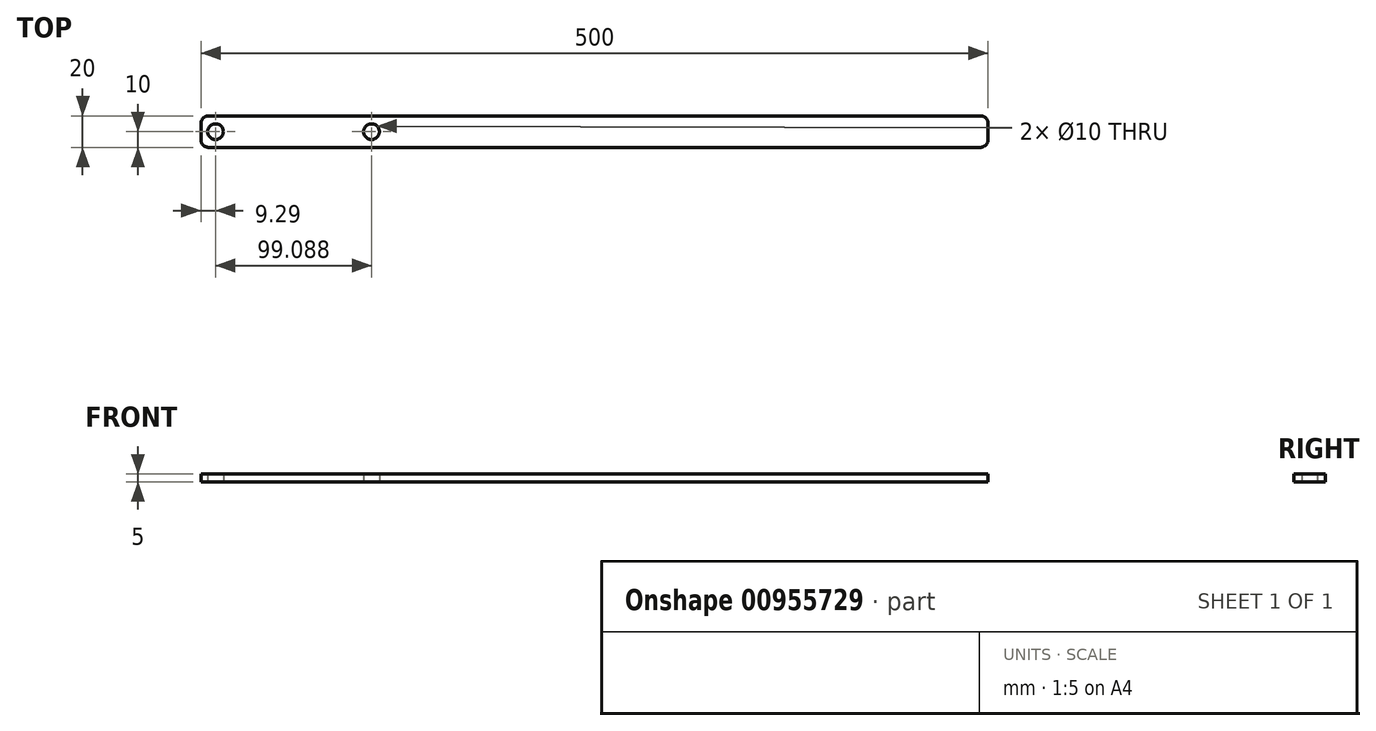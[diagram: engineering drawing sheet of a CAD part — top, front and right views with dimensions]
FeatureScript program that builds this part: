
annotation { "Feature Type Name" : "Feature", "Feature Type Description" : "" }
export const myFeature = defineFeature(function(context is Context, id is Id, definition is map)
    precondition{}
    {
        {
            var Q0;
            Q0=qCreatedBy(makeId("Top.planeOp"),FACE);
            var sketch = newSketch(context, id + "F0", { "sketchPlane" : qUnion([Q0])});
            skLineSegment(sketch, "E0.bottom", {"start": v(250, -10) * mm, "end": v(-250, -10) * mm});
            skLineSegment(sketch, "E0.top", {"start": v(250, 10) * mm, "end": v(-250, 10) * mm});
            skLineSegment(sketch, "E0.left", {"start": v(250, -10) * mm, "end": v(250, 10) * mm});
            skLineSegment(sketch, "E0.right", {"start": v(-250, -10) * mm, "end": v(-250, 10) * mm});
            skPoint(sketch, "E0.middle", {"position": v(0, 0) * mm});
            skCircle(sketch, "E1", {"center": v(-141.62, 0) * mm, "radius": 5 * mm});
            skCircle(sketch, "E2", {"center": v(-240.7, 0) * mm, "radius": 5 * mm});
            skSolve(sketch);
        }
        {
            var Q0;
            Q0=makeQuery(id+"F0.imprint","IMPRINT",FACE,{"disambiguationData":[TD([[makeQuery(id+"F0.imprint","IMPRINT",EDGE,{"derivedFrom":sQuery(id+"F0.wireOp",EDGE,"E0.bottom")}),-1.0]])]});
            extrude(context, id + "F1", {"entities" : qUnion([Q0]), "depth" : 5 * mm, "offsetDistance" : 25 * mm});
        }
        {
            var Q0;
            Q0=makeQuery(id+"F1.opExtrude","SWEPT_EDGE",EDGE,{"disambiguationData":[OSD([sQuery(id+"F0.wireOp",EDGE,"E0.bottom"),sQuery(id+"F0.wireOp",EDGE,"E0.left")])]});
            var Q1;
            Q1=makeQuery(id+"F1.opExtrude","SWEPT_EDGE",EDGE,{"disambiguationData":[OSD([sQuery(id+"F0.wireOp",EDGE,"E0.top"),sQuery(id+"F0.wireOp",EDGE,"E0.left")])]});
            var Q2;
            Q2=makeQuery(id+"F1.opExtrude","SWEPT_EDGE",EDGE,{"disambiguationData":[OSD([sQuery(id+"F0.wireOp",EDGE,"E0.bottom"),sQuery(id+"F0.wireOp",EDGE,"E0.right")])]});
            var Q3;
            Q3=makeQuery(id+"F1.opExtrude","SWEPT_EDGE",EDGE,{"disambiguationData":[OSD([sQuery(id+"F0.wireOp",EDGE,"E0.top"),sQuery(id+"F0.wireOp",EDGE,"E0.right")])]});
            fillet(context, id + "F2", {"entities" : qUnion([Q0, Q1, Q2, Q3]), "radius" : 5 * mm, "tangentPropagation" : true, "allowEdgeOverflow" : false});
        }
    });
